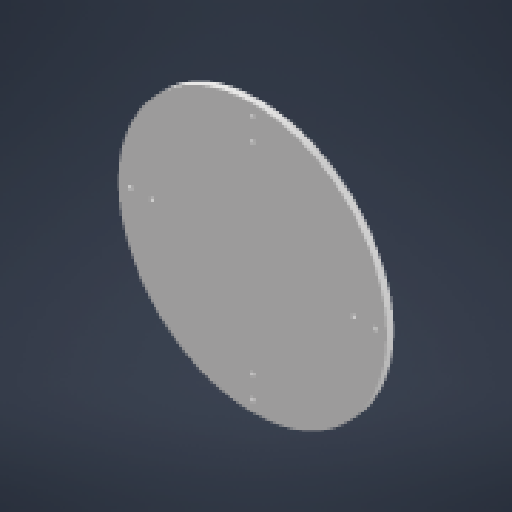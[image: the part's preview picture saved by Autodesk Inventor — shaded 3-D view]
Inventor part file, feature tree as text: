
AUTODESK INVENTOR PART (.ipt)
format: ipt  version: 2023 (Build 270158000, 158)  size: 192,000 bytes
history: native  units: mm
features: extrude x2, sketch x2
ambient origin geometry x8: Origin, YZ Plane, XZ Plane, XY Plane, X Axis, Y Axis, Z Axis, Center Point
bodies: Solid1 (feature_tree)
feature tree (4):
  extrude  "Extrusion1"  Depth=3.0mm
  extrude  "Extrusion2"  Depth=5.0mm TaperAngle=0.0deg
  sketch  "Sketch1"  dims[d0=200.0mm d2=3.0mm]
  sketch  "Sketch2"  dims[d3=40.0mm d5=360.0deg d7=5.0mm d8=0.0mm d10=3.0mm d11=3.0mm d12=3.0mm d13=3.0mm d15=11.0mm d16=11.0mm d17=11.0mm d18=11.0mm d19=3.0mm d20=0.0mm]
